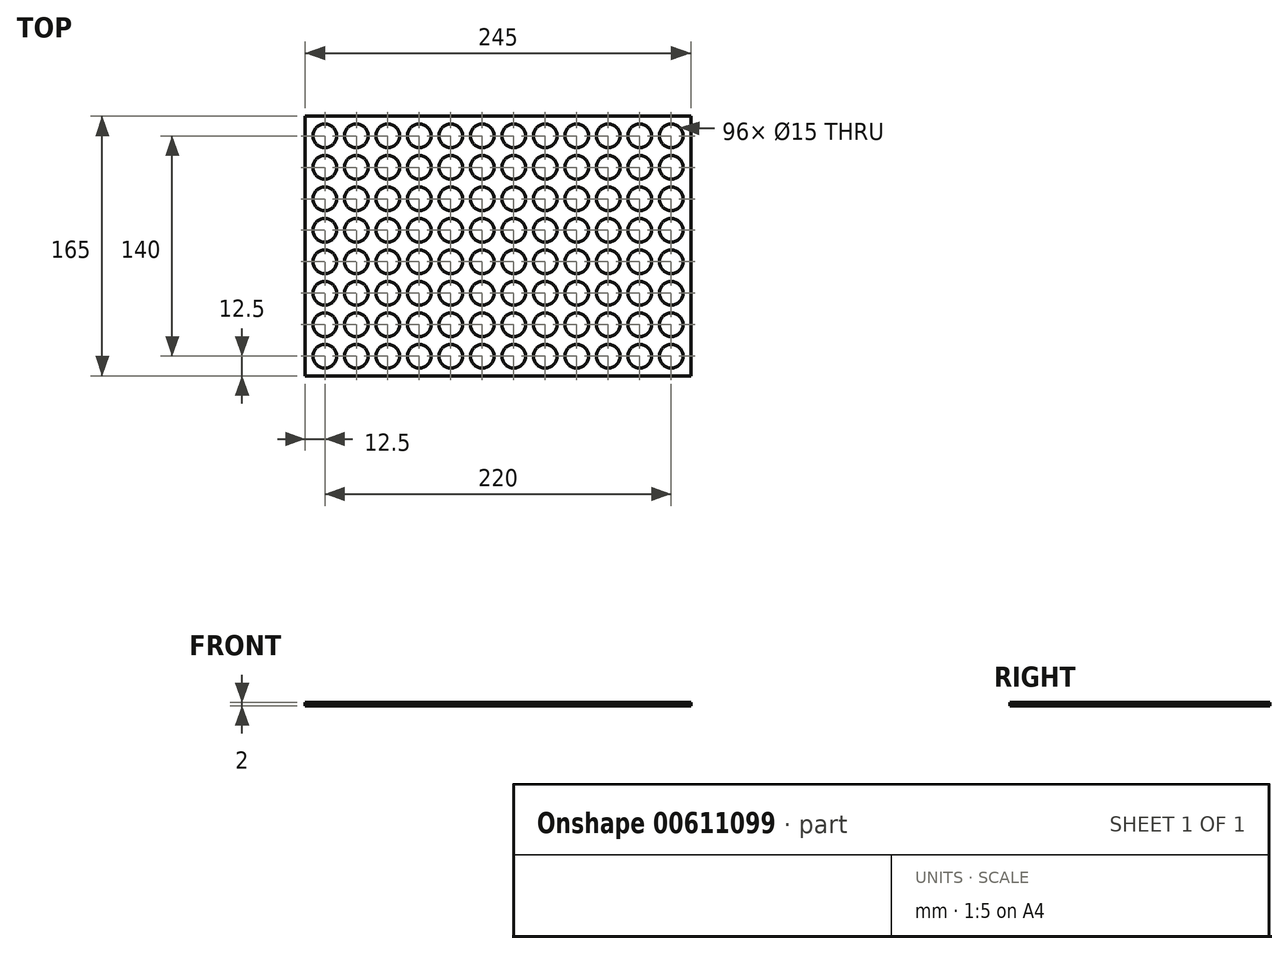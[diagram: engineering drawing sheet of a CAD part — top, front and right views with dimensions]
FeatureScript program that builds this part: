
annotation { "Feature Type Name" : "Feature", "Feature Type Description" : "" }
export const myFeature = defineFeature(function(context is Context, id is Id, definition is map)
    precondition{}
    {
        {
            var Q0;
            Q0=qCreatedBy(makeId("Top.planeOp"),FACE);
            var sketch = newSketch(context, id + "F0", { "sketchPlane" : qUnion([Q0])});
            skCircle(sketch, "E0", {"center": v(-110, -70) * mm, "radius": 7.5 * mm});
            skLineSegment(sketch, "E1", {"start": v(0, 0) * mm, "end": v(0, 123.6) * mm, "construction": true});
            skCircle(sketch, "E2.1.0.0", {"center": v(-90, -70) * mm, "radius": 7.5 * mm});
            skCircle(sketch, "E2.2.0.0", {"center": v(-70, -70) * mm, "radius": 7.5 * mm});
            skCircle(sketch, "E2.3.0.0", {"center": v(-50, -70) * mm, "radius": 7.5 * mm});
            skCircle(sketch, "E2.4.0.0", {"center": v(-30, -70) * mm, "radius": 7.5 * mm});
            skCircle(sketch, "E2.5.0.0", {"center": v(-10, -70) * mm, "radius": 7.5 * mm});
            skCircle(sketch, "E2.6.0.0", {"center": v(10, -70) * mm, "radius": 7.5 * mm});
            skCircle(sketch, "E2.7.0.0", {"center": v(30, -70) * mm, "radius": 7.5 * mm});
            skCircle(sketch, "E2.8.0.0", {"center": v(50, -70) * mm, "radius": 7.5 * mm});
            skCircle(sketch, "E2.9.0.0", {"center": v(70, -70) * mm, "radius": 7.5 * mm});
            skCircle(sketch, "E2.10.0.0", {"center": v(90, -70) * mm, "radius": 7.5 * mm});
            skCircle(sketch, "E2.11.0.0", {"center": v(110, -70) * mm, "radius": 7.5 * mm});
            skLineSegment(sketch, "E2.direction1", {"start": v(-110, -70) * mm, "end": v(-90, -70) * mm, "construction": true});
            skLineSegment(sketch, "E2.direction2", {"start": v(-110, -70) * mm, "end": v(-110, -50) * mm, "construction": true});
            skCircle(sketch, "E3.0.0.1", {"center": v(-110, -50) * mm, "radius": 7.5 * mm});
            skCircle(sketch, "E3.0.0.2", {"center": v(-110, -30) * mm, "radius": 7.5 * mm});
            skCircle(sketch, "E3.0.0.3", {"center": v(-110, -10) * mm, "radius": 7.5 * mm});
            skCircle(sketch, "E3.0.0.4", {"center": v(-110, 10) * mm, "radius": 7.5 * mm});
            skCircle(sketch, "E3.0.0.5", {"center": v(-110, 30) * mm, "radius": 7.5 * mm});
            skCircle(sketch, "E3.0.0.6", {"center": v(-110, 50) * mm, "radius": 7.5 * mm});
            skCircle(sketch, "E3.0.0.7", {"center": v(-110, 70) * mm, "radius": 7.5 * mm});
            skCircle(sketch, "E3.0.1.1", {"center": v(-90, -50) * mm, "radius": 7.5 * mm});
            skCircle(sketch, "E3.0.1.2", {"center": v(-90, -30) * mm, "radius": 7.5 * mm});
            skCircle(sketch, "E3.0.1.3", {"center": v(-90, -10) * mm, "radius": 7.5 * mm});
            skCircle(sketch, "E3.0.1.4", {"center": v(-90, 10) * mm, "radius": 7.5 * mm});
            skCircle(sketch, "E3.0.1.5", {"center": v(-90, 30) * mm, "radius": 7.5 * mm});
            skCircle(sketch, "E3.0.1.6", {"center": v(-90, 50) * mm, "radius": 7.5 * mm});
            skCircle(sketch, "E3.0.1.7", {"center": v(-90, 70) * mm, "radius": 7.5 * mm});
            skCircle(sketch, "E3.0.2.1", {"center": v(-70, -50) * mm, "radius": 7.5 * mm});
            skCircle(sketch, "E3.0.2.2", {"center": v(-70, -30) * mm, "radius": 7.5 * mm});
            skCircle(sketch, "E3.0.2.3", {"center": v(-70, -10) * mm, "radius": 7.5 * mm});
            skCircle(sketch, "E3.0.2.4", {"center": v(-70, 10) * mm, "radius": 7.5 * mm});
            skCircle(sketch, "E3.0.2.5", {"center": v(-70, 30) * mm, "radius": 7.5 * mm});
            skCircle(sketch, "E3.0.2.6", {"center": v(-70, 50) * mm, "radius": 7.5 * mm});
            skCircle(sketch, "E3.0.2.7", {"center": v(-70, 70) * mm, "radius": 7.5 * mm});
            skCircle(sketch, "E3.0.3.1", {"center": v(-50, -50) * mm, "radius": 7.5 * mm});
            skCircle(sketch, "E3.0.3.2", {"center": v(-50, -30) * mm, "radius": 7.5 * mm});
            skCircle(sketch, "E3.0.3.3", {"center": v(-50, -10) * mm, "radius": 7.5 * mm});
            skCircle(sketch, "E3.0.3.4", {"center": v(-50, 10) * mm, "radius": 7.5 * mm});
            skCircle(sketch, "E3.0.3.5", {"center": v(-50, 30) * mm, "radius": 7.5 * mm});
            skCircle(sketch, "E3.0.3.6", {"center": v(-50, 50) * mm, "radius": 7.5 * mm});
            skCircle(sketch, "E3.0.3.7", {"center": v(-50, 70) * mm, "radius": 7.5 * mm});
            skCircle(sketch, "E3.0.4.1", {"center": v(-30, -50) * mm, "radius": 7.5 * mm});
            skCircle(sketch, "E3.0.4.2", {"center": v(-30, -30) * mm, "radius": 7.5 * mm});
            skCircle(sketch, "E3.0.4.3", {"center": v(-30, -10) * mm, "radius": 7.5 * mm});
            skCircle(sketch, "E3.0.4.4", {"center": v(-30, 10) * mm, "radius": 7.5 * mm});
            skCircle(sketch, "E3.0.4.5", {"center": v(-30, 30) * mm, "radius": 7.5 * mm});
            skCircle(sketch, "E3.0.4.6", {"center": v(-30, 50) * mm, "radius": 7.5 * mm});
            skCircle(sketch, "E3.0.4.7", {"center": v(-30, 70) * mm, "radius": 7.5 * mm});
            skCircle(sketch, "E3.0.5.1", {"center": v(-10, -50) * mm, "radius": 7.5 * mm});
            skCircle(sketch, "E3.0.5.2", {"center": v(-10, -30) * mm, "radius": 7.5 * mm});
            skCircle(sketch, "E3.0.5.3", {"center": v(-10, -10) * mm, "radius": 7.5 * mm});
            skCircle(sketch, "E3.0.5.4", {"center": v(-10, 10) * mm, "radius": 7.5 * mm});
            skCircle(sketch, "E3.0.5.5", {"center": v(-10, 30) * mm, "radius": 7.5 * mm});
            skCircle(sketch, "E3.0.5.6", {"center": v(-10, 50) * mm, "radius": 7.5 * mm});
            skCircle(sketch, "E3.0.5.7", {"center": v(-10, 70) * mm, "radius": 7.5 * mm});
            skCircle(sketch, "E3.0.6.1", {"center": v(10, -50) * mm, "radius": 7.5 * mm});
            skCircle(sketch, "E3.0.6.2", {"center": v(10, -30) * mm, "radius": 7.5 * mm});
            skCircle(sketch, "E3.0.6.3", {"center": v(10, -10) * mm, "radius": 7.5 * mm});
            skCircle(sketch, "E3.0.6.4", {"center": v(10, 10) * mm, "radius": 7.5 * mm});
            skCircle(sketch, "E3.0.6.5", {"center": v(10, 30) * mm, "radius": 7.5 * mm});
            skCircle(sketch, "E3.0.6.6", {"center": v(10, 50) * mm, "radius": 7.5 * mm});
            skCircle(sketch, "E3.0.6.7", {"center": v(10, 70) * mm, "radius": 7.5 * mm});
            skCircle(sketch, "E3.0.7.1", {"center": v(30, -50) * mm, "radius": 7.5 * mm});
            skCircle(sketch, "E3.0.7.2", {"center": v(30, -30) * mm, "radius": 7.5 * mm});
            skCircle(sketch, "E3.0.7.3", {"center": v(30, -10) * mm, "radius": 7.5 * mm});
            skCircle(sketch, "E3.0.7.4", {"center": v(30, 10) * mm, "radius": 7.5 * mm});
            skCircle(sketch, "E3.0.7.5", {"center": v(30, 30) * mm, "radius": 7.5 * mm});
            skCircle(sketch, "E3.0.7.6", {"center": v(30, 50) * mm, "radius": 7.5 * mm});
            skCircle(sketch, "E3.0.7.7", {"center": v(30, 70) * mm, "radius": 7.5 * mm});
            skCircle(sketch, "E3.0.8.1", {"center": v(50, -50) * mm, "radius": 7.5 * mm});
            skCircle(sketch, "E3.0.8.2", {"center": v(50, -30) * mm, "radius": 7.5 * mm});
            skCircle(sketch, "E3.0.8.3", {"center": v(50, -10) * mm, "radius": 7.5 * mm});
            skCircle(sketch, "E3.0.8.4", {"center": v(50, 10) * mm, "radius": 7.5 * mm});
            skCircle(sketch, "E3.0.8.5", {"center": v(50, 30) * mm, "radius": 7.5 * mm});
            skCircle(sketch, "E3.0.8.6", {"center": v(50, 50) * mm, "radius": 7.5 * mm});
            skCircle(sketch, "E3.0.8.7", {"center": v(50, 70) * mm, "radius": 7.5 * mm});
            skCircle(sketch, "E3.0.9.1", {"center": v(70, -50) * mm, "radius": 7.5 * mm});
            skCircle(sketch, "E3.0.9.2", {"center": v(70, -30) * mm, "radius": 7.5 * mm});
            skCircle(sketch, "E3.0.9.3", {"center": v(70, -10) * mm, "radius": 7.5 * mm});
            skCircle(sketch, "E3.0.9.4", {"center": v(70, 10) * mm, "radius": 7.5 * mm});
            skCircle(sketch, "E3.0.9.5", {"center": v(70, 30) * mm, "radius": 7.5 * mm});
            skCircle(sketch, "E3.0.9.6", {"center": v(70, 50) * mm, "radius": 7.5 * mm});
            skCircle(sketch, "E3.0.9.7", {"center": v(70, 70) * mm, "radius": 7.5 * mm});
            skCircle(sketch, "E3.0.10.1", {"center": v(90, -50) * mm, "radius": 7.5 * mm});
            skCircle(sketch, "E3.0.10.2", {"center": v(90, -30) * mm, "radius": 7.5 * mm});
            skCircle(sketch, "E3.0.10.3", {"center": v(90, -10) * mm, "radius": 7.5 * mm});
            skCircle(sketch, "E3.0.10.4", {"center": v(90, 10) * mm, "radius": 7.5 * mm});
            skCircle(sketch, "E3.0.10.5", {"center": v(90, 30) * mm, "radius": 7.5 * mm});
            skCircle(sketch, "E3.0.10.6", {"center": v(90, 50) * mm, "radius": 7.5 * mm});
            skCircle(sketch, "E3.0.10.7", {"center": v(90, 70) * mm, "radius": 7.5 * mm});
            skCircle(sketch, "E3.0.11.1", {"center": v(110, -50) * mm, "radius": 7.5 * mm});
            skCircle(sketch, "E3.0.11.2", {"center": v(110, -30) * mm, "radius": 7.5 * mm});
            skCircle(sketch, "E3.0.11.3", {"center": v(110, -10) * mm, "radius": 7.5 * mm});
            skCircle(sketch, "E3.0.11.4", {"center": v(110, 10) * mm, "radius": 7.5 * mm});
            skCircle(sketch, "E3.0.11.5", {"center": v(110, 30) * mm, "radius": 7.5 * mm});
            skCircle(sketch, "E3.0.11.6", {"center": v(110, 50) * mm, "radius": 7.5 * mm});
            skCircle(sketch, "E3.0.11.7", {"center": v(110, 70) * mm, "radius": 7.5 * mm});
            skLineSegment(sketch, "E4", {"start": v(0, 0) * mm, "end": v(142.8, 0) * mm, "construction": true});
            skLineSegment(sketch, "E5.bottom", {"start": v(122.5, 82.5) * mm, "end": v(-122.5, 82.5) * mm});
            skLineSegment(sketch, "E5.top", {"start": v(122.5, -82.5) * mm, "end": v(-122.5, -82.5) * mm});
            skLineSegment(sketch, "E5.left", {"start": v(122.5, 82.5) * mm, "end": v(122.5, -82.5) * mm});
            skLineSegment(sketch, "E5.right", {"start": v(-122.5, 82.5) * mm, "end": v(-122.5, -82.5) * mm});
            skPoint(sketch, "E5.middle", {"position": v(0, 0) * mm});
            skSolve(sketch);
        }
        {
            var Q0;
            Q0=makeQuery(id+"F0.imprint","IMPRINT",FACE,{"disambiguationData":[TD([[makeQuery(id+"F0.imprint","IMPRINT",EDGE,{"derivedFrom":sQuery(id+"F0.wireOp",EDGE,"E0")}),-1.0]])]});
            extrude(context, id + "F1", {"entities" : qUnion([Q0]), "depth" : 2 * mm, "offsetDistance" : 25 * mm});
        }
    });
